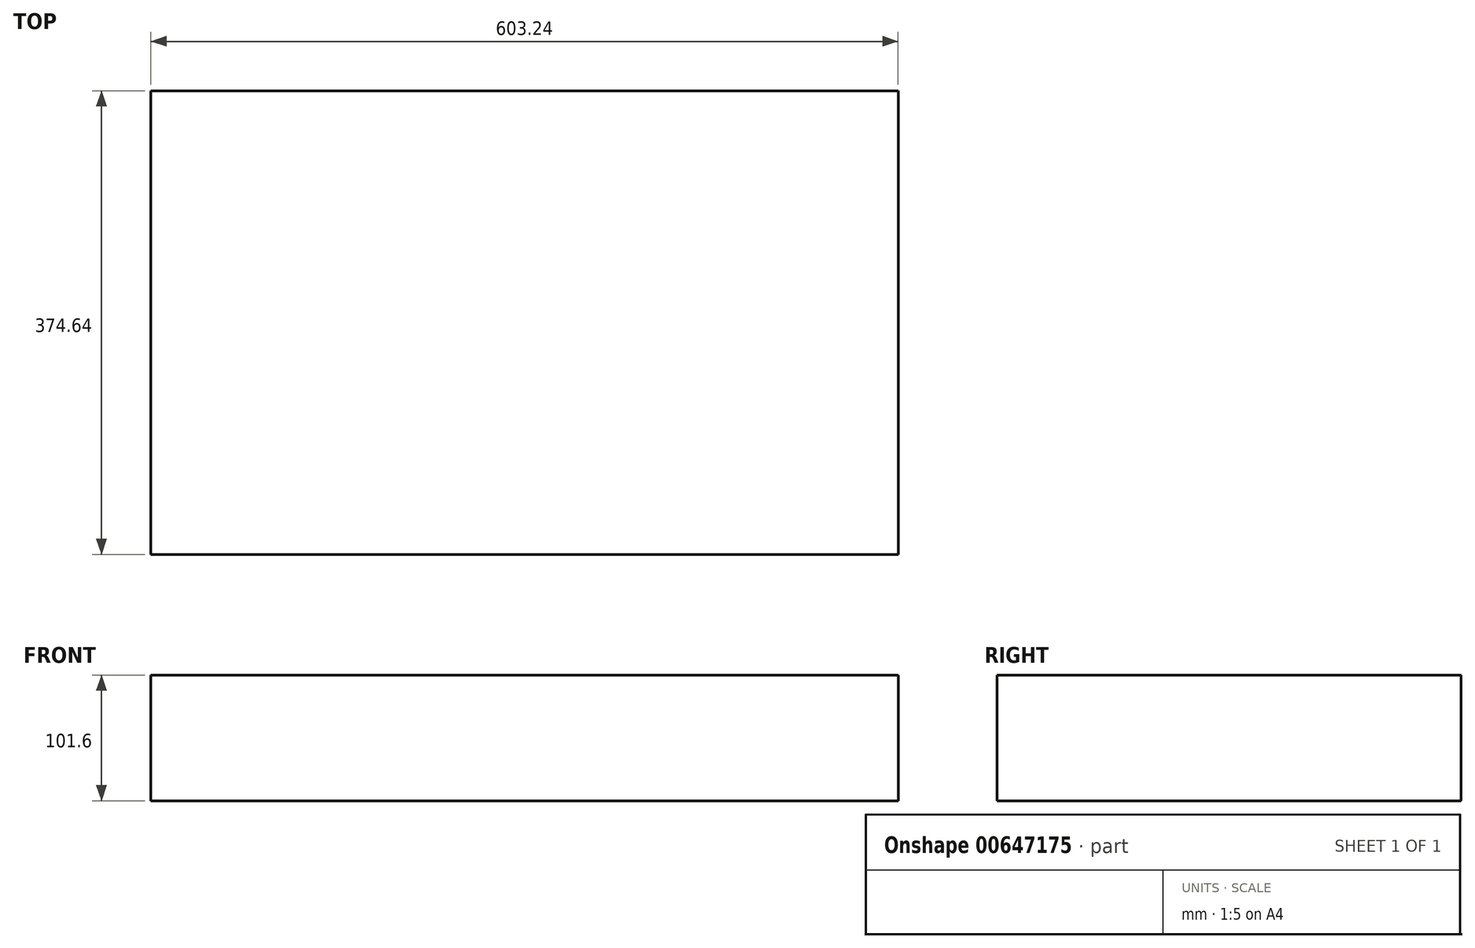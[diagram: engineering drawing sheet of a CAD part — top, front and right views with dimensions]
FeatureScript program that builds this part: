
annotation { "Feature Type Name" : "Feature", "Feature Type Description" : "" }
export const myFeature = defineFeature(function(context is Context, id is Id, definition is map)
    precondition{}
    {
        {
            var Q0;
            Q0=qCreatedBy(makeId("Top.planeOp"),FACE);
            var sketch = newSketch(context, id + "F0", { "sketchPlane" : qUnion([Q0])});
            skLineSegment(sketch, "E0.bottom", {"start": v(-301.62, 187.32) * mm, "end": v(301.63, 187.32) * mm});
            skLineSegment(sketch, "E0.top", {"start": v(-301.63, -187.33) * mm, "end": v(301.63, -187.33) * mm});
            skLineSegment(sketch, "E0.left", {"start": v(-301.62, 187.32) * mm, "end": v(-301.63, -187.33) * mm});
            skLineSegment(sketch, "E0.right", {"start": v(301.63, 187.32) * mm, "end": v(301.63, -187.33) * mm});
            skPoint(sketch, "E0.middle", {"position": v(0, 0) * mm});
            skSolve(sketch);
        }
        {
            var Q0;
            Q0=makeQuery(id+"F0.imprint","IMPRINT",FACE,{"disambiguationData":[TD([[makeQuery(id+"F0.imprint","IMPRINT",EDGE,{"derivedFrom":sQuery(id+"F0.wireOp",EDGE,"E0.bottom")}),-1.0]])]});
            extrude(context, id + "F1", {"entities" : qUnion([Q0]), "depth" : 101.6 * mm, "offsetDistance" : 25.4 * mm});
        }
    });
